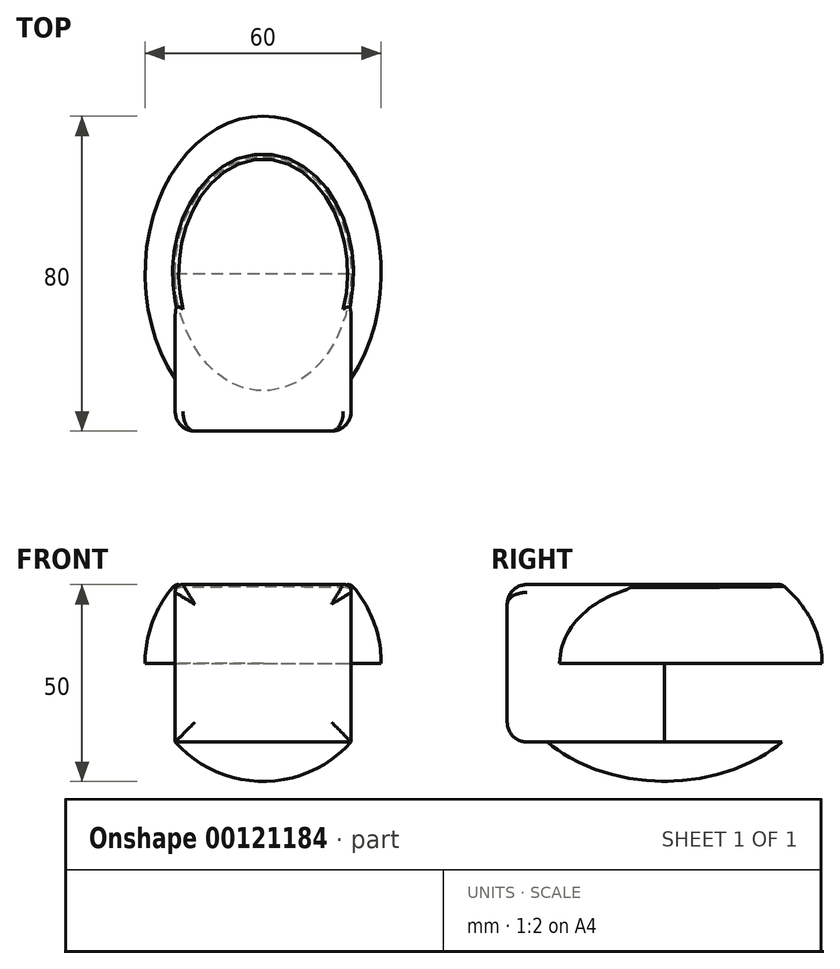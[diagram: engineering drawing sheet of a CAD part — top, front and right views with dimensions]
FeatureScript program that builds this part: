
annotation { "Feature Type Name" : "Feature", "Feature Type Description" : "" }
export const myFeature = defineFeature(function(context is Context, id is Id, definition is map)
    precondition{}
    {
        {
            var Q0;
            Q0=qCreatedBy(makeId("Top.planeOp"),FACE);
            var sketch = newSketch(context, id + "F0", { "sketchPlane" : qUnion([Q0])});
            skEllipse(sketch, "E0", {"center": v(0, 0) * mm, "majorRadius": 40 * mm, "minorRadius": 30 * mm, "majorAxis": v(0, 1)});
            skPoint(sketch, "E1", {"position": v(0, -40) * mm});
            skPoint(sketch, "E2", {"position": v(0, 40) * mm});
            skLineSegment(sketch, "E3", {"start": v(0, 40) * mm, "end": v(0, -40) * mm});
            skPoint(sketch, "E4", {"position": v(-30, 0) * mm});
            skPoint(sketch, "E5", {"position": v(30, 0) * mm});
            skSolve(sketch);
        }
        {
            var Q0;
            Q0=qCreatedBy(makeId("Right.planeOp"),FACE);
            var sketch = newSketch(context, id + "F1", { "sketchPlane" : qUnion([Q0])});
            skEllipse(sketch, "E6", {"center": v(0, 0) * mm, "majorRadius": 40 * mm, "minorRadius": 30 * mm, "majorAxis": v(-1, 0)});
            skLineSegment(sketch, "E7", {"start": v(0, 20) * mm, "end": v(0, -20) * mm});
            skPoint(sketch, "E8", {"position": v(-40, 0) * mm});
            skPoint(sketch, "E9", {"position": v(40, 0) * mm});
            skLineSegment(sketch, "E10", {"start": v(-40, 0) * mm, "end": v(40, 0) * mm});
            skPoint(sketch, "E11", {"position": v(0, 30) * mm});
            skPoint(sketch, "E12", {"position": v(0, -30) * mm});
            skLineSegment(sketch, "E13", {"start": v(29.81, 20) * mm, "end": v(-29.81, 20) * mm});
            skLineSegment(sketch, "E14", {"start": v(29.81, -20) * mm, "end": v(-29.81, -20) * mm});
            skLineSegment(sketch, "E15", {"start": v(0, 30) * mm, "end": v(0, -30) * mm});
            skSolve(sketch);
        }
        {
            var Q0;
            {var subQ0=sQuery(id+"F1.wireOp",EDGE,"E10");var subQ1=sQuery(id+"F1.wireOp",EDGE,"E6");var subQ2=makeQuery(id+"F1.imprint","INTERSECT",VERTEX,{"disambiguationData":[OD(0.0)],"derivedFrom":[subQ1,subQ0]});Q0=makeQuery(id+"F1.imprint","IMPRINT",FACE,{"disambiguationData":[TD([[makeQuery(id+"F1.imprint","IMPRINT",EDGE,{"disambiguationData":[TD([[subQ2,1.0]])],"derivedFrom":subQ1}),1.0]])]});}
            var Q1;
            {var subQ0=sQuery(id+"F1.wireOp",EDGE,"E10");var subQ1=sQuery(id+"F1.wireOp",EDGE,"E6");var subQ2=makeQuery(id+"F1.imprint","INTERSECT",VERTEX,{"disambiguationData":[OD(1.0)],"derivedFrom":[subQ1,subQ0]});Q1=makeQuery(id+"F1.imprint","IMPRINT",FACE,{"disambiguationData":[TD([[makeQuery(id+"F1.imprint","IMPRINT",EDGE,{"disambiguationData":[TD([[subQ2,-1.0]])],"derivedFrom":subQ1}),1.0]])]});}
            var Q2;
            {var subQ0=sQuery(id+"F1.wireOp",EDGE,"E13");var subQ1=sQuery(id+"F1.wireOp",EDGE,"E6");var subQ2=makeQuery(id+"F1.imprint","INTERSECT",VERTEX,{"disambiguationData":[OD(0.0)],"derivedFrom":[subQ1,subQ0]});Q2=makeQuery(id+"F1.imprint","IMPRINT",FACE,{"disambiguationData":[TD([[makeQuery(id+"F1.imprint","IMPRINT",EDGE,{"disambiguationData":[TD([[subQ2,-1.0]])],"derivedFrom":subQ1}),1.0]])]});}
            var Q3;
            {var subQ0=sQuery(id+"F1.wireOp",EDGE,"E13");var subQ1=sQuery(id+"F1.wireOp",EDGE,"E6");var subQ2=makeQuery(id+"F1.imprint","INTERSECT",VERTEX,{"disambiguationData":[OD(1.0)],"derivedFrom":[subQ1,subQ0]});Q3=makeQuery(id+"F1.imprint","IMPRINT",FACE,{"disambiguationData":[TD([[makeQuery(id+"F1.imprint","IMPRINT",EDGE,{"disambiguationData":[TD([[subQ2,1.0]])],"derivedFrom":subQ1}),1.0]])]});}
            var Q4;
            Q4=sQuery(id+"F1.wireOp",EDGE,"E10");
            revolve(context, id + "F2", {"entities" : qUnion([Q0, Q1, Q2, Q3]), "axis" : qUnion([Q4]), "revolveType" : RevolveType.FULL});
        }
        {
            var Q0;
            {var subQ0=sQuery(id+"F1.wireOp",EDGE,"E13");var subQ1=sQuery(id+"F1.wireOp",EDGE,"E6");var subQ2=makeQuery(id+"F1.imprint","INTERSECT",VERTEX,{"disambiguationData":[OD(0.0)],"derivedFrom":[subQ1,subQ0]});Q0=makeQuery(id+"F1.imprint","IMPRINT",FACE,{"disambiguationData":[TD([[makeQuery(id+"F1.imprint","IMPRINT",EDGE,{"disambiguationData":[TD([[subQ2,-1.0]])],"derivedFrom":subQ1}),1.0]])]});}
            var Q1;
            {var subQ0=sQuery(id+"F1.wireOp",EDGE,"E14");var subQ1=sQuery(id+"F1.wireOp",EDGE,"E6");var subQ2=makeQuery(id+"F1.imprint","INTERSECT",VERTEX,{"disambiguationData":[OD(0.0)],"derivedFrom":[subQ1,subQ0]});Q1=makeQuery(id+"F1.imprint","IMPRINT",FACE,{"disambiguationData":[TD([[makeQuery(id+"F1.imprint","IMPRINT",EDGE,{"disambiguationData":[TD([[subQ2,1.0]])],"derivedFrom":subQ1}),1.0]])]});}
            var Q2;
            Q2=sQuery(id+"F1.wireOp",EDGE,"E7");
            revolve(context, id + "F3", {"operationType" : NewBodyOperationType.REMOVE, "entities" : qUnion([Q0, Q1]), "axis" : qUnion([Q2]), "revolveType" : RevolveType.FULL, "oppositeDirection" : true});
        }
        {
            var Q0;
            Q0=qCreatedBy(makeId("Front.planeOp"),FACE);
            cPlane(context, id + "F4", {"entities" : qUnion([Q0]), "cplaneType" : CPlaneType.OFFSET, "offset" : 40 * mm, "width" : 150 * mm, "height" : 150 * mm});
        }
        {
            var Q0;
            Q0=qCreatedBy(id+"F4.planeOp",FACE);
            var sketch = newSketch(context, id + "F5", { "sketchPlane" : qUnion([Q0])});
            skLineSegment(sketch, "E16.bottom", {"start": v(-22.36, 20) * mm, "end": v(22.36, 20) * mm});
            skLineSegment(sketch, "E16.top", {"start": v(-22.36, -20) * mm, "end": v(22.36, -20) * mm});
            skLineSegment(sketch, "E16.left", {"start": v(-22.36, 20) * mm, "end": v(-22.36, -20) * mm});
            skLineSegment(sketch, "E16.right", {"start": v(22.36, 20) * mm, "end": v(22.36, -20) * mm});
            skPoint(sketch, "E16.middle", {"position": v(0, 0) * mm});
            skSolve(sketch);
        }
        {
            var Q0;
            Q0=makeQuery(id+"F5.imprint","IMPRINT",FACE,{"disambiguationData":[TD([[makeQuery(id+"F5.imprint","IMPRINT",EDGE,{"derivedFrom":sQuery(id+"F5.wireOp",EDGE,"E16.bottom")}),-1.0]])]});
            extrude(context, id + "F6", {"entities" : qUnion([Q0]), "operationType" : NewBodyOperationType.ADD, "oppositeDirection" : true, "depth" : 40 * mm});
        }
        {
            var Q0;
            Q0=makeQuery(id+"F6.opExtrude","CAP_EDGE",EDGE,{"disambiguationData":[OSD([sQuery(id+"F5.wireOp",EDGE,"E16.bottom")])],"isStart":true});
            var Q1;
            Q1=makeQuery(id+"F6.opExtrude","CAP_EDGE",EDGE,{"disambiguationData":[OSD([sQuery(id+"F5.wireOp",EDGE,"E16.right")])],"isStart":true});
            var Q2;
            Q2=makeQuery(id+"F6.opExtrude","CAP_EDGE",EDGE,{"disambiguationData":[OSD([sQuery(id+"F5.wireOp",EDGE,"E16.left")])],"isStart":true});
            var Q3;
            Q3=makeQuery(id+"F6.opExtrude","CAP_EDGE",EDGE,{"disambiguationData":[OSD([sQuery(id+"F5.wireOp",EDGE,"E16.top")])],"isStart":true});
            fillet(context, id + "F7", {"entities" : qUnion([Q0, Q1, Q2, Q3]), "radius" : 5 * mm, "tangentPropagation" : true, "allowEdgeOverflow" : false});
        }
        {
            var Q0;
            Q0=makeQuery(id+"F6.boolean.opBoolean","MERGE",FACE,{"derivedFrom":[makeQuery(id+"F3.boolean.opBoolean","COPY",FACE,{"derivedFrom":makeQuery(id+"F3.opRevolve","SWEPT_FACE",FACE,{"disambiguationData":[OSD([sQuery(id+"F1.wireOp",EDGE,"E13")])]})}),makeQuery(id+"F6.opExtrude","SWEPT_FACE",FACE,{"disambiguationData":[OSD([sQuery(id+"F5.wireOp",EDGE,"E16.bottom")])]})]});
            fillet(context, id + "F8", {"entities" : qUnion([Q0]), "radius" : 2 * mm, "tangentPropagation" : true, "rho" : 0.5, "crossSection" : FilletCrossSection.CONIC, "allowEdgeOverflow" : false});
        }
    });
